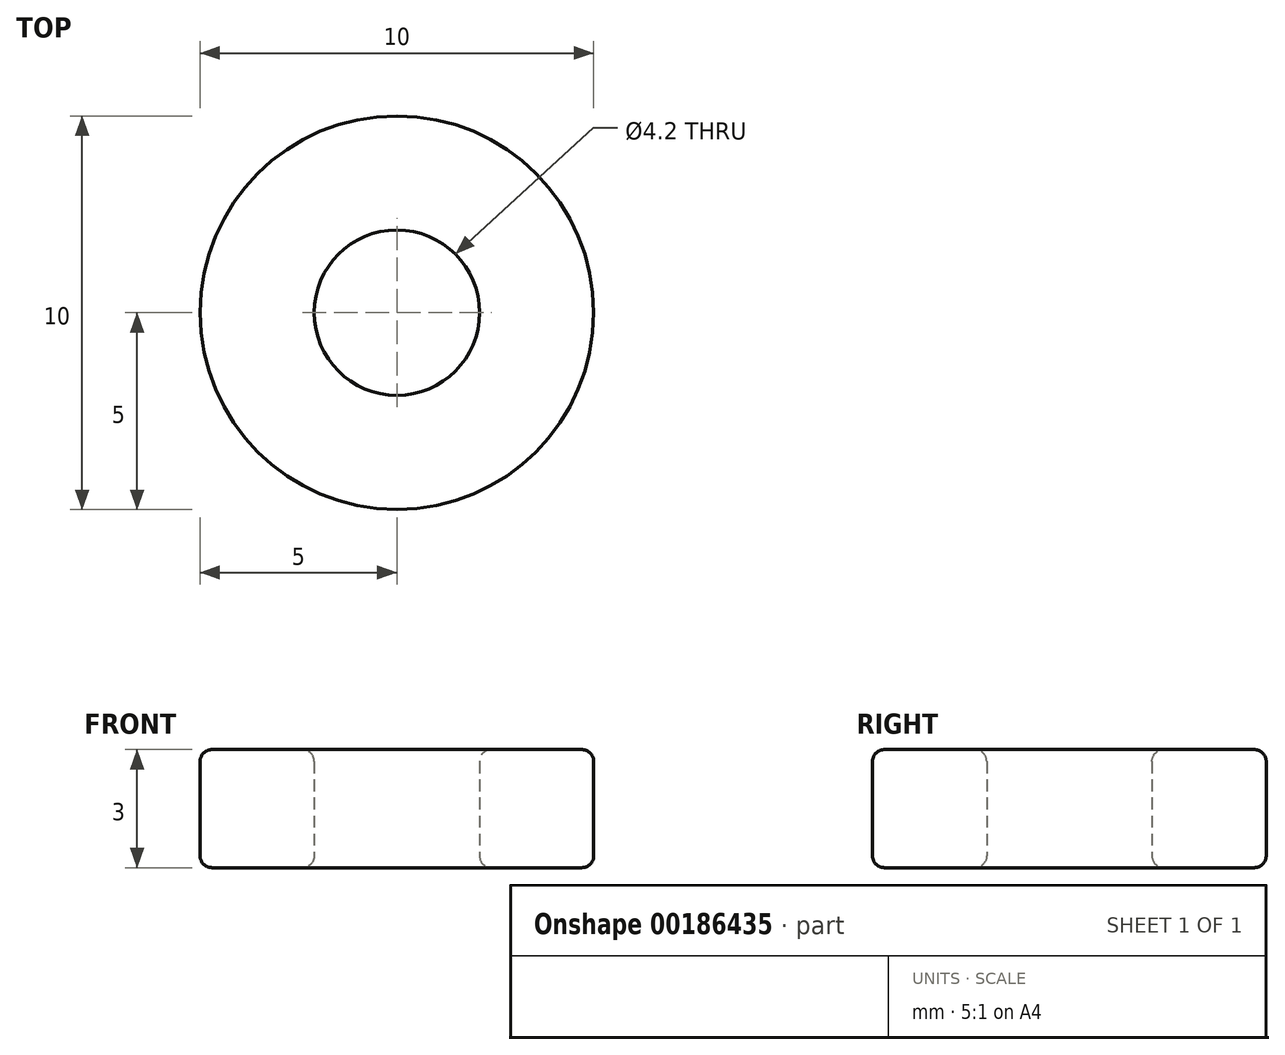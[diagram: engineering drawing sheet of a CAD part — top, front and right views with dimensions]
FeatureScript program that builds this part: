
annotation { "Feature Type Name" : "Feature", "Feature Type Description" : "" }
export const myFeature = defineFeature(function(context is Context, id is Id, definition is map)
    precondition{}
    {
        {
            var Q0;
            Q0=qCreatedBy(makeId("Top.planeOp"),FACE);
            var sketch = newSketch(context, id + "F0", { "sketchPlane" : qUnion([Q0])});
            skCircle(sketch, "E0", {"center": v(0, 0) * mm, "radius": 2.1 * mm});
            skCircle(sketch, "E1", {"center": v(0, 0) * mm, "radius": 5 * mm});
            skSolve(sketch);
        }
        {
            var Q0;
            Q0=makeQuery(id+"F0.imprint","IMPRINT",FACE,{"disambiguationData":[TD([[makeQuery(id+"F0.imprint","IMPRINT",EDGE,{"derivedFrom":sQuery(id+"F0.wireOp",EDGE,"E0")}),-1.0]])]});
            extrude(context, id + "F1", {"entities" : qUnion([Q0]), "depth" : 3 * mm});
        }
        {
            var Q0;
            Q0=makeQuery(id+"F1.opExtrude","CAP_EDGE",EDGE,{"disambiguationData":[OSD([sQuery(id+"F0.wireOp",EDGE,"E1")])],"isStart":false});
            var Q1;
            Q1=makeQuery(id+"F1.opExtrude","CAP_EDGE",EDGE,{"disambiguationData":[OSD([sQuery(id+"F0.wireOp",EDGE,"E1")])],"isStart":true});
            var Q2;
            Q2=makeQuery(id+"F1.opExtrude","CAP_EDGE",EDGE,{"disambiguationData":[OSD([sQuery(id+"F0.wireOp",EDGE,"E0")])],"isStart":false});
            var Q3;
            Q3=makeQuery(id+"F1.opExtrude","CAP_EDGE",EDGE,{"disambiguationData":[OSD([sQuery(id+"F0.wireOp",EDGE,"E0")])],"isStart":true});
            fillet(context, id + "F2", {"entities" : qUnion([Q0, Q1, Q2, Q3]), "radius" : .3 * mm, "tangentPropagation" : true, "allowEdgeOverflow" : false});
        }
    });
